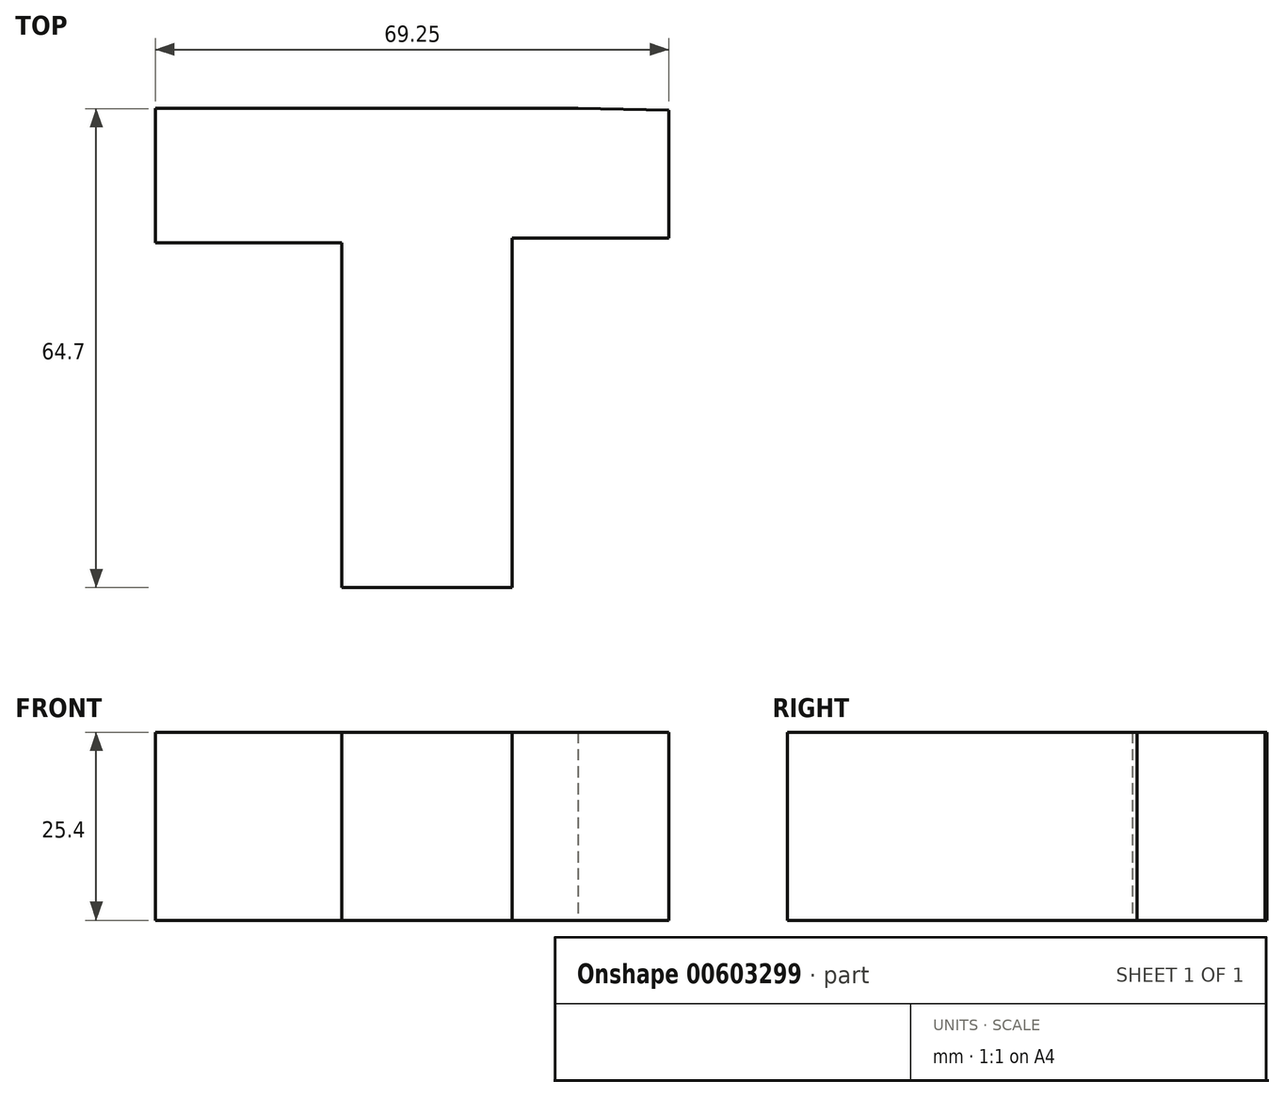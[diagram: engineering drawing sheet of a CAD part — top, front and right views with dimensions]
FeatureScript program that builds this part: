
annotation { "Feature Type Name" : "Feature", "Feature Type Description" : "" }
export const myFeature = defineFeature(function(context is Context, id is Id, definition is map)
    precondition{}
    {
        {
            var Q0;
            Q0=qCreatedBy(makeId("Top.planeOp"),FACE);
            var sketch = newSketch(context, id + "F0", { "sketchPlane" : qUnion([Q0])});
            skLineSegment(sketch, "E0", {"start": v(0, 0) * mm, "end": v(-11.34, 0) * mm});
            skLineSegment(sketch, "E1", {"start": v(-11.34, 0) * mm, "end": v(-11.34, 46.55) * mm});
            skLineSegment(sketch, "E2", {"start": v(-11.34, 46.55) * mm, "end": v(-36.46, 46.55) * mm});
            skLineSegment(sketch, "E3", {"start": v(-36.46, 46.55) * mm, "end": v(-36.46, 64.7) * mm});
            skLineSegment(sketch, "E4", {"start": v(-36.46, 64.7) * mm, "end": v(20.54, 64.7) * mm});
            skLineSegment(sketch, "E5", {"start": v(0, 0) * mm, "end": v(11.68, 0) * mm});
            skLineSegment(sketch, "E6", {"start": v(11.68, 0) * mm, "end": v(11.68, 47.18) * mm});
            skLineSegment(sketch, "E7", {"start": v(11.68, 47.18) * mm, "end": v(32.79, 47.18) * mm});
            skLineSegment(sketch, "E8", {"start": v(32.79, 47.18) * mm, "end": v(32.79, 64.5) * mm});
            skLineSegment(sketch, "E9", {"start": v(32.79, 64.5) * mm, "end": v(20.54, 64.7) * mm});
            skSolve(sketch);
        }
        {
            var Q0;
            Q0=makeQuery(id+"F0.imprint","IMPRINT",FACE,{"disambiguationData":[TD([[makeQuery(id+"F0.imprint","IMPRINT",EDGE,{"derivedFrom":sQuery(id+"F0.wireOp",EDGE,"E0")}),-1.0]])]});
            extrude(context, id + "F1", {"entities" : qUnion([Q0]), "depth" : 25.4 * mm, "offsetDistance" : 25.4 * mm});
        }
    });
